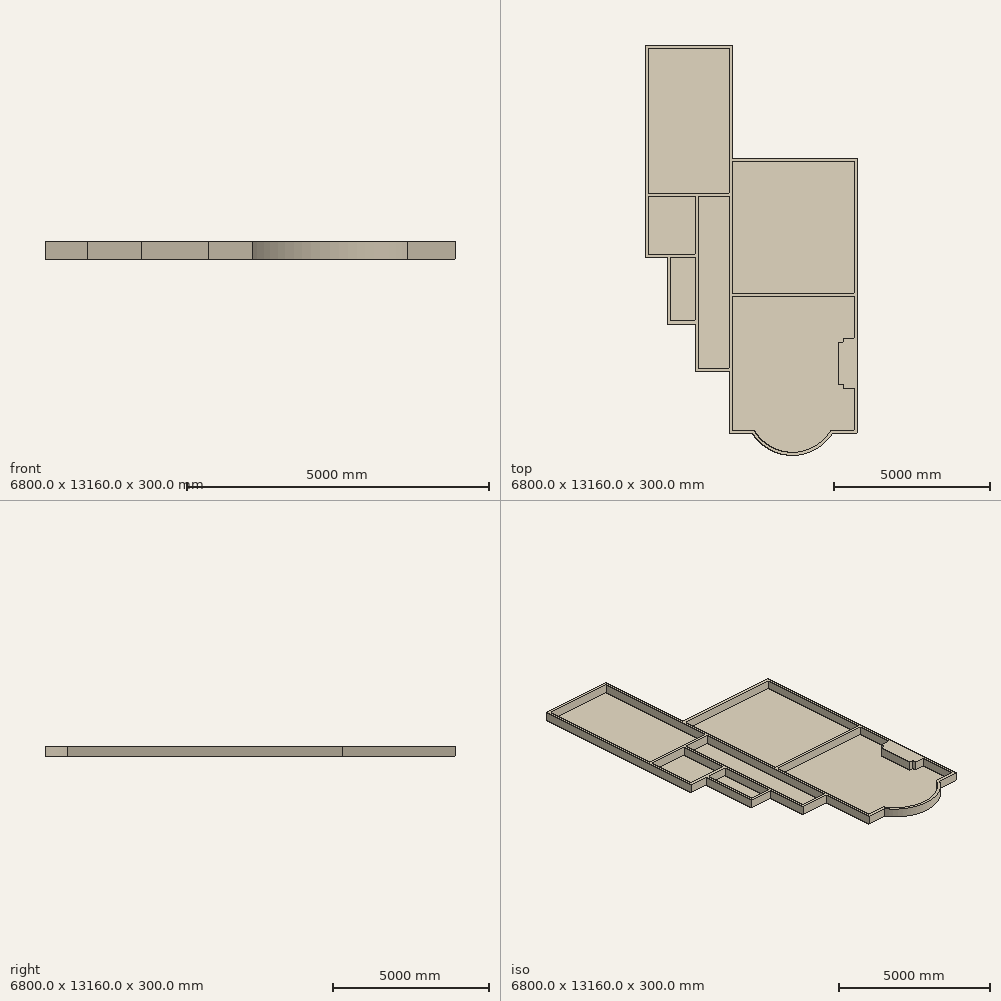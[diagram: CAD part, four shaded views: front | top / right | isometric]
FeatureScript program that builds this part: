
annotation { "Feature Type Name" : "Feature", "Feature Type Description" : "" }
export const myFeature = defineFeature(function(context is Context, id is Id, definition is map)
    precondition{}
    {
        {
            var Q0;
            Q0=qCreatedBy(makeId("Top.planeOp"),FACE);
            var sketch = newSketch(context, id + "F0", { "sketchPlane" : qUnion([Q0])});
            skLineSegment(sketch, "E0", {"start": v(0, 0) * mm, "end": v(0, 5497.27) * mm});
            skLineSegment(sketch, "E1", {"start": v(0, 5497.27) * mm, "end": v(1000, 5497.27) * mm});
            skLineSegment(sketch, "E2", {"start": v(1000, 5497.27) * mm, "end": v(1000, 0) * mm});
            skLineSegment(sketch, "E3", {"start": v(1000, 0) * mm, "end": v(0, 0) * mm});
            skLineSegment(sketch, "E4.bottom", {"start": v(1100, 6640) * mm, "end": v(5000, 6640) * mm});
            skLineSegment(sketch, "E4.top", {"start": v(1100, 2410) * mm, "end": v(5000, 2410) * mm});
            skLineSegment(sketch, "E4.left", {"start": v(1100, 6640) * mm, "end": v(1100, 2410) * mm});
            skLineSegment(sketch, "E4.right", {"start": v(5000, 6640) * mm, "end": v(5000, 2410) * mm});
            skLineSegment(sketch, "E5.bottom", {"start": v(1100, 2310) * mm, "end": v(5000, 2310) * mm});
            skLineSegment(sketch, "E5.left", {"start": v(1100, 2310) * mm, "end": v(1100, -2000) * mm});
            skLineSegment(sketch, "E5.right", {"start": v(5000, 2310) * mm, "end": v(5000, 960) * mm});
            skLineSegment(sketch, "E6.bottom", {"start": v(1000, 5597.27) * mm, "end": v(-1600, 5597.27) * mm});
            skLineSegment(sketch, "E6.top", {"start": v(1000, 10260) * mm, "end": v(-1600, 10260) * mm});
            skLineSegment(sketch, "E6.left", {"start": v(1000, 5597.27) * mm, "end": v(1000, 10260) * mm});
            skLineSegment(sketch, "E6.right", {"start": v(-1600, 5597.27) * mm, "end": v(-1600, 10260) * mm});
            skLineSegment(sketch, "E7.bottom", {"start": v(-1600, 5497.27) * mm, "end": v(-100, 5497.27) * mm});
            skLineSegment(sketch, "E7.top", {"start": v(-1600, 3660) * mm, "end": v(-100, 3660) * mm});
            skLineSegment(sketch, "E7.left", {"start": v(-1600, 5497.27) * mm, "end": v(-1600, 3660) * mm});
            skLineSegment(sketch, "E7.right", {"start": v(-100, 5497.27) * mm, "end": v(-100, 3660) * mm});
            skLineSegment(sketch, "E8.bottom", {"start": v(-900, 3560) * mm, "end": v(-100, 3560) * mm});
            skLineSegment(sketch, "E8.top", {"start": v(-900, 1518.24) * mm, "end": v(-100, 1518.24) * mm});
            skLineSegment(sketch, "E8.left", {"start": v(-900, 3560) * mm, "end": v(-900, 1518.24) * mm});
            skLineSegment(sketch, "E8.right", {"start": v(-100, 3560) * mm, "end": v(-100, 1518.24) * mm});
            skLineSegment(sketch, "E9", {"start": v(5000, 2410) * mm, "end": v(5000, 2310) * mm, "construction": true});
            skLineSegment(sketch, "E10", {"start": v(1100, 2410) * mm, "end": v(1100, 2310) * mm, "construction": true});
            skLineSegment(sketch, "E11", {"start": v(-1600, 5497.27) * mm, "end": v(-1600, 5597.27) * mm, "construction": true});
            skLineSegment(sketch, "E12", {"start": v(-100, 3660) * mm, "end": v(-100, 3560) * mm, "construction": true});
            skLineSegment(sketch, "E13", {"start": v(-1700, 10360) * mm, "end": v(1100, 10360) * mm});
            skLineSegment(sketch, "E14", {"start": v(1100, 10360) * mm, "end": v(1100, 6740) * mm});
            skLineSegment(sketch, "E15", {"start": v(1100, 6740) * mm, "end": v(5100, 6740) * mm});
            skLineSegment(sketch, "E16", {"start": v(5100, 6740) * mm, "end": v(5100, -2100) * mm});
            skLineSegment(sketch, "E17", {"start": v(5100, -2100) * mm, "end": v(4305.65, -2100) * mm});
            skLineSegment(sketch, "E18", {"start": v(-1700, 10360) * mm, "end": v(-1700, 3560) * mm});
            skLineSegment(sketch, "E19", {"start": v(-1700, 3560) * mm, "end": v(-1000, 3560) * mm});
            skLineSegment(sketch, "E20", {"start": v(-1000, 3560) * mm, "end": v(-1000, 1418.24) * mm});
            skLineSegment(sketch, "E21", {"start": v(1100, 6740) * mm, "end": v(1100, 6640) * mm, "construction": true});
            skLineSegment(sketch, "E22", {"start": v(-900, 3560) * mm, "end": v(-1000, 3560) * mm, "construction": true});
            skLineSegment(sketch, "E23", {"start": v(-1000, 1418.24) * mm, "end": v(-100, 1418.24) * mm});
            skLineSegment(sketch, "E24", {"start": v(-100, 1418.24) * mm, "end": v(-100, -100) * mm});
            skLineSegment(sketch, "E25", {"start": v(-100, -100) * mm, "end": v(1000, -100) * mm});
            skLineSegment(sketch, "E26", {"start": v(1000, -100) * mm, "end": v(1000, -2100) * mm});
            skLineSegment(sketch, "E27", {"start": v(1000, -2100) * mm, "end": v(1734.35, -2100) * mm});
            skLineSegment(sketch, "E28", {"start": v(1000, 0) * mm, "end": v(1000, -100) * mm, "construction": true});
            skLineSegment(sketch, "E29", {"start": v(-100, 1518.24) * mm, "end": v(-100, 1418.24) * mm, "construction": true});
            skLineSegment(sketch, "E30", {"start": v(0, 5497.27) * mm, "end": v(-100, 5497.27) * mm, "construction": true});
            skLineSegment(sketch, "E31", {"start": v(1000, 5597.27) * mm, "end": v(1000, 5497.27) * mm, "construction": true});
            skLineSegment(sketch, "E32", {"start": v(3020, -2000) * mm, "end": v(3020, -2100) * mm, "construction": true});
            skLineSegment(sketch, "E33", {"start": v(1000, 0) * mm, "end": v(1100, 0) * mm, "construction": true});
            skLineSegment(sketch, "E34", {"start": v(5000, 2410) * mm, "end": v(5100, 2410) * mm, "construction": true});
            skLineSegment(sketch, "E35", {"start": v(-1600, 10260) * mm, "end": v(-1700, 10260) * mm, "construction": true});
            skLineSegment(sketch, "E36", {"start": v(-1600, 10260) * mm, "end": v(-1600, 10360) * mm, "construction": true});
            skLineSegment(sketch, "E37", {"start": v(5100, 155) * mm, "end": v(1000, 155) * mm, "construction": true});
            skPoint(sketch, "E37.startSnap0", {"position": v(5000, 155) * mm});
            skLineSegment(sketch, "E38", {"start": v(5000, 960) * mm, "end": v(4640, 960) * mm});
            skLineSegment(sketch, "E39", {"start": v(4640, 960) * mm, "end": v(4640, 820) * mm});
            skLineSegment(sketch, "E40", {"start": v(4640, 820) * mm, "end": v(4500, 820) * mm});
            skLineSegment(sketch, "E41", {"start": v(4500, 820) * mm, "end": v(4500, 155) * mm});
            skLineSegment(sketch, "E42.trimOffspring", {"start": v(5000, -650) * mm, "end": v(5000, -2000) * mm});
            skLineSegment(sketch, "E43.MirrorCS", {"start": v(4500, -510) * mm, "end": v(4500, 155) * mm});
            skLineSegment(sketch, "E44.MirrorCS", {"start": v(4640, -510) * mm, "end": v(4500, -510) * mm});
            skLineSegment(sketch, "E45.MirrorCS", {"start": v(4640, -650) * mm, "end": v(4640, -510) * mm});
            skLineSegment(sketch, "E46.MirrorCS", {"start": v(5000, -650) * mm, "end": v(4640, -650) * mm});
            skArc(sketch, "E47", {"start": v(1790, -2000) * mm, "mid": v(3020, -2700) * mm, "end": v(4250, -2000) * mm});
            skArc(sketch, "E48", {"start": v(1734.35, -2100) * mm, "mid": v(3020, -2800) * mm, "end": v(4305.65, -2100) * mm});
            skLineSegment(sketch, "E49", {"start": v(5000, -2000) * mm, "end": v(4250, -2000) * mm});
            skLineSegment(sketch, "E50", {"start": v(1100, -2000) * mm, "end": v(1790, -2000) * mm});
            skLineSegment(sketch, "E51", {"start": v(1790, -2000) * mm, "end": v(4250, -2000) * mm, "construction": true});
            skLineSegment(sketch, "E52", {"start": v(1734.35, -2100) * mm, "end": v(4305.65, -2100) * mm, "construction": true});
            skLineSegment(sketch, "E53", {"start": v(3020, -2100) * mm, "end": v(3020, -2700) * mm, "construction": true});
            skLineSegment(sketch, "E54", {"start": v(3020, -2700) * mm, "end": v(3020, -2800) * mm, "construction": true});
            skSolve(sketch);
        }
        {
            var Q0;
            Q0 = qSketchRegion(id + "F0", true);
            extrude(context, id + "F1", {"entities" : qUnion([Q0]), "depth" : 300 * mm, "offsetDistance" : 25 * mm});
        }
        {
            var Q0;
            Q0=qCreatedBy(makeId("Top.planeOp"),FACE);
            var sketch = newSketch(context, id + "F2", { "sketchPlane" : qUnion([Q0])});
            skArc(sketch, "E55.0", {"start": v(4305.65, -2100) * mm, "mid": v(3020, -2800) * mm, "end": v(1734.35, -2100) * mm});
            skLineSegment(sketch, "E55.1", {"start": v(5100, -2100) * mm, "end": v(4305.65, -2100) * mm});
            skLineSegment(sketch, "E55.2", {"start": v(5100, 6740) * mm, "end": v(5100, -2100) * mm});
            skLineSegment(sketch, "E55.3", {"start": v(-100, 1418.24) * mm, "end": v(-1000, 1418.24) * mm});
            skLineSegment(sketch, "E55.4", {"start": v(-100, -100) * mm, "end": v(-100, 1418.24) * mm});
            skLineSegment(sketch, "E55.5", {"start": v(1000, -100) * mm, "end": v(-100, -100) * mm});
            skLineSegment(sketch, "E55.6", {"start": v(1000, -2100) * mm, "end": v(1000, -100) * mm});
            skLineSegment(sketch, "E55.7", {"start": v(-1000, 1418.24) * mm, "end": v(-1000, 3560) * mm});
            skLineSegment(sketch, "E55.8", {"start": v(-1000, 3560) * mm, "end": v(-1700, 3560) * mm});
            skLineSegment(sketch, "E55.9", {"start": v(-1700, 3560) * mm, "end": v(-1700, 10360) * mm});
            skLineSegment(sketch, "E55.10", {"start": v(1734.35, -2100) * mm, "end": v(1000, -2100) * mm});
            skLineSegment(sketch, "E55.11", {"start": v(-1700, 10360) * mm, "end": v(1100, 10360) * mm});
            skLineSegment(sketch, "E55.12", {"start": v(1100, 10360) * mm, "end": v(1100, 6740) * mm});
            skLineSegment(sketch, "E55.13", {"start": v(1100, 6740) * mm, "end": v(5100, 6740) * mm});
            skSolve(sketch);
        }
        {
            var Q0;
            Q0 = qSketchRegion(id + "F2", true);
            extrude(context, id + "F3", {"entities" : qUnion([Q0]), "operationType" : NewBodyOperationType.ADD, "depth" : 1 * mm, "offsetDistance" : 25 * mm});
        }
    });
